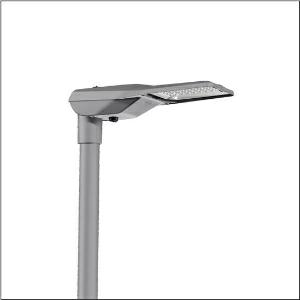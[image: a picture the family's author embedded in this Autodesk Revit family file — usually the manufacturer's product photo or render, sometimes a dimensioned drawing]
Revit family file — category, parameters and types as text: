
# Revit family: streetlight_sl_21_iq_mini___st0_8a_5xe2c31y08gb_e7ef
name_source: partatom
category: Lighting Fixtures
units: mm (PartAtom-declared; Revit-internal decimal feet)

## family parameters
Cut with Voids When Loaded = No
Host = Face
Light Source = No
Part Type = Normal
Room Calculation Point = No
Round Connector Dimension = Use Diameter
Shared = No

## types (1)
- --- (1 x LED, 5990 lm, 39.8 W, 3000K)
    Apparent Load = 40 VA
    CIE Flux Codes = 38 75 97 100 100
    Color Rendering = 70
    Color Temperature = 3000K
    Default Elevation = 1800 mm
    Description = Streetlight SL 21 iQ mini, mast luminaire, primary light control with lens, of PMMA, primary optical cover: cover, of toughened safety glass, transparent, light distribution: ST0.8a, light emission: direct distribution, primary light characteristic: asymmetric, installation type: post-top, side-entry, LED, High Power LED, rated luminous flux: 5.990lm, luminous efficacy: 151lm/W, light colour: 730, colour temperature: 3000K, control: pre-setting: logarithmic dimming characteristic, Street-Remote, Auto-Match, Temp-Guard, Lumen-Switch, Night-Set, Smart-Wire, Light-Fading, Desk-Remote (wireless, voltage-free reading and setting of iQ features in the workshop via application-optimized NFC function/RFID function), optimised constant luminous flux control (CLO 2.0), mains connection: 220..240V, AC, 50/60Hz, start of lifetime: 40W, end of service life: 41W, reduction: 18W, luminaire housing, of diecast aluminium, powder-coated, Siteco® metallic grey (DB 702S), corrosivity category C5 mid according to DIN EN ISO 12944, please order mast flange separately, inclination adjustable: 0°, 5°, 10°, 15°, sealing non-destructively replaceable, multi-level sealing system, length: 628mm, width: 235mm, height: 110mm, mast flange for spigot size: 42mm (side-entry): 5XC10008XM4, 60/48mm (side-entry/post-top): 5XC10108XM2, 76/60mm (side-entry/post-top): 5XC10108XM1, Smart Interface below and above, protection rating (complete): IP66, insulation class (complete): insulation class II (safety insulation), certification: CE, ENEC, ENEC+, VDE, impact resistance: IK09, permissible operating ambient temperature for outdoor applications: -40..+50°C, standard-compliant lighting for roads and squares, packaging unit: 1 piece

Light Distribution: ST0.8a
    Height = 110 mm
    Lamp = 1 x LED
    Lamp Light Flux = 5990 lm
    Lamp Power = 39.8 W
    Lamp count = 1
    Length = 625 mm
    Luminous efficacy = 151 lm/W
    Manufacturer = Siteco
    ModVariant = No
    Model = 5XE2C31Y08GB
    Number of Poles = 1
    OnlyDefault = Yes
    Power Factor = 1
    Product Name = Streetlight SL 21 iQ mini | ST0.8a
    Product group = mast luminaire | pylon top
    ProductGroupID = 6100
    Protection Class = Protection class II
    Protection Degree = IP 66
    RLX_Detail_Level = 1
    RLX_Emergency_Light_Flux = 0 lm
    RLX_Emergency_Type = 0
    RLX_Emergency_Type_DB = No
    RlxData = <blob elided: 92725 chars, md5=9461d88d>
    Socket = socket
    Standby Power = 0 W
    System Light Flux = 5990 lm
    System Power = 40 W
    Type Comments = factory setting: luminous flux: 100 % | dim-lin: 254 | 800 mA
    Type Image = l_1003514.jpg
    URL = http://relux.com
    VarID = @adj_082193
    Voltage = 0 V
    Weight = 0.00 kg
    Width = 234 mm

## geometry (parser evidence)
native form markers: Blend x4, Sweep x11
no freeform markers — native parametric forms only
